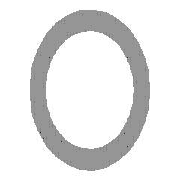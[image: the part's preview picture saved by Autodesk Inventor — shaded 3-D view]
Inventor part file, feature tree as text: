
AUTODESK INVENTOR PART (.ipt)
format: ipt  version: 2021 (Build 250183000, 183)  size: 205,312 bytes
history: native  units: mm (DEFAULTED — no unit token found)
features: other x5, plane x2, sketch x2, sweep x1
ambient origin geometry x8: Origin, YZ Plane, XZ Plane, XY Plane, X Axis, Y Axis, Z Axis, Center Point
bodies: Solid1 (feature_tree)
feature tree (10):
  parser-record x1  (decoder bookkeeping rows leaked as tree rows — omitted from the tree; the rows remain in map.json)
  other  "Driven Length"
  other  "Plano inicial"
  other  "Plano final"
  other  "Trayectoria de barrido"
  plane  "Plano de trabajo de orientación"
  sweep  "Cuerpo"
  sketch  "Sketch3"  dims[d0=21.336mm d1=3.7338mm]
  plane  "Work Plane3"
  sketch  "Sketch4"  dims[d4=-0.0mm d5=575.800269mm d6=90.0deg d7=575.800269mm d8=0.0mm d9=0.0mm]
